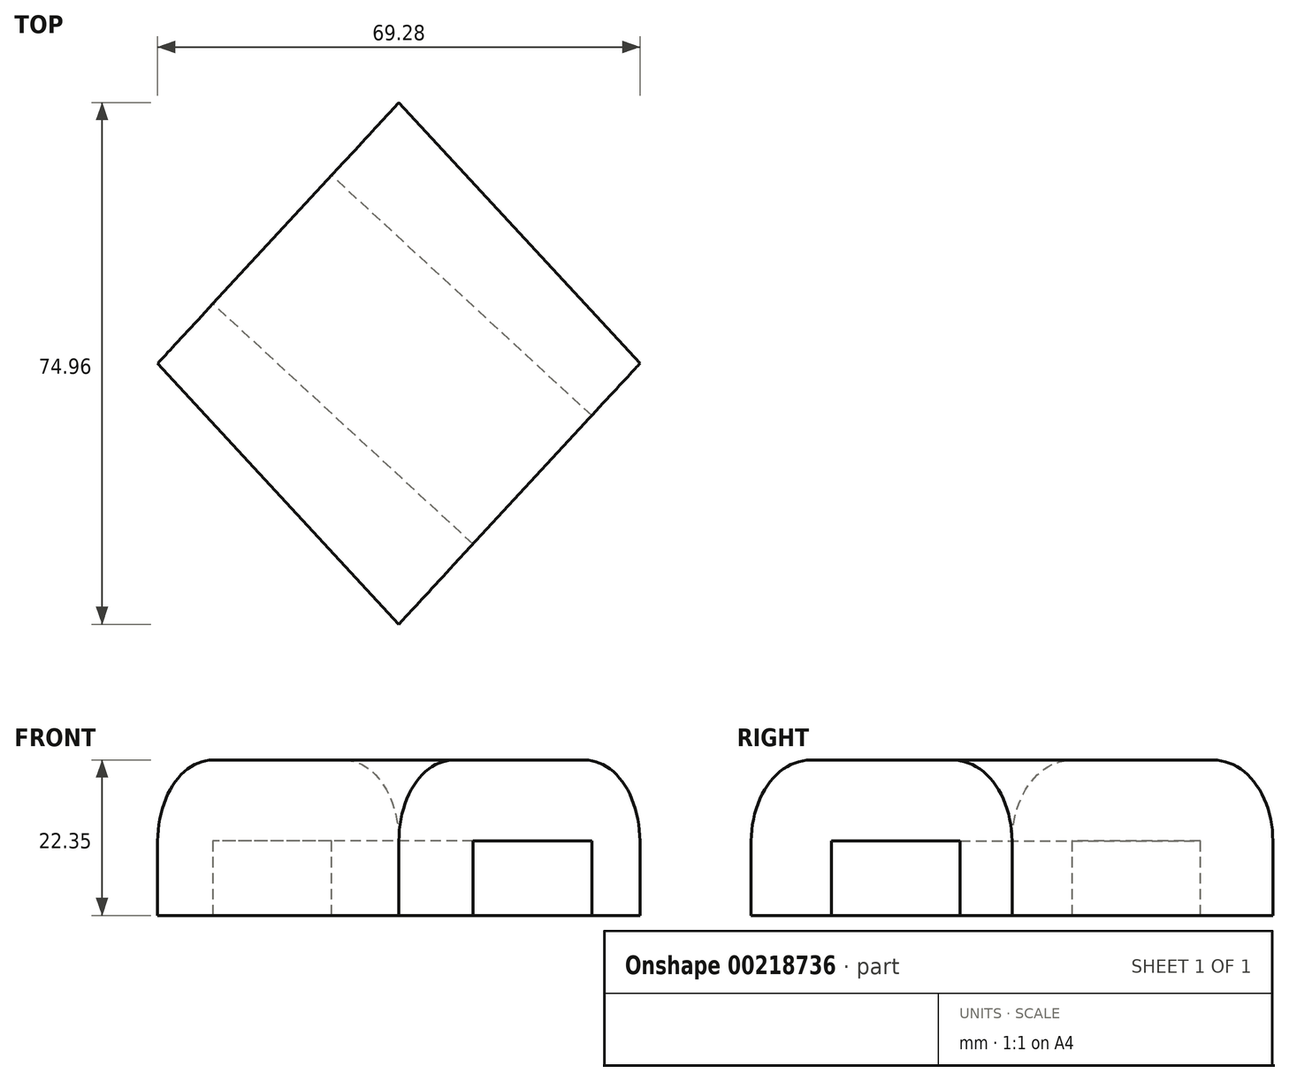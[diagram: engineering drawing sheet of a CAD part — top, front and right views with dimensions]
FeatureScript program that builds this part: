
annotation { "Feature Type Name" : "Feature", "Feature Type Description" : "" }
export const myFeature = defineFeature(function(context is Context, id is Id, definition is map)
    precondition{}
    {
        {
            var Q0;
            Q0=qCreatedBy(makeId("Top.planeOp"),FACE);
            var sketch = newSketch(context, id + "F0", { "sketchPlane" : qUnion([Q0])});
            skLineSegment(sketch, "E0", {"start": v(-34.64, 0) * mm, "end": v(0, 37.48) * mm});
            skLineSegment(sketch, "E1", {"start": v(0, 37.48) * mm, "end": v(34.64, 0) * mm});
            skLineSegment(sketch, "E2", {"start": v(34.64, 0) * mm, "end": v(0, -37.48) * mm});
            skLineSegment(sketch, "E3", {"start": v(0, -37.48) * mm, "end": v(-34.64, 0) * mm});
            skSolve(sketch);
        }
        {
            var Q0;
            Q0=makeQuery(id+"F0.imprint","IMPRINT",FACE,{"disambiguationData":[TD([[makeQuery(id+"F0.imprint","IMPRINT",EDGE,{"derivedFrom":sQuery(id+"F0.wireOp",EDGE,"E0")}),-1.0]])]});
            extrude(context, id + "F1", {"entities" : qUnion([Q0]), "depth" : 22.35 * mm});
        }
        {
            var Q0;
            Q0=makeQuery(id+"F1.opExtrude","CAP_EDGE",EDGE,{"disambiguationData":[OSD([sQuery(id+"F0.wireOp",EDGE,"E3")])],"isStart":false});
            var Q1;
            Q1=makeQuery(id+"F1.opExtrude","CAP_EDGE",EDGE,{"disambiguationData":[OSD([sQuery(id+"F0.wireOp",EDGE,"E1")])],"isStart":false});
            fillet(context, id + "F2", {"entities" : qUnion([Q0, Q1]), "radius" : 11.65 * mm, "tangentPropagation" : true, "allowEdgeOverflow" : false});
        }
        {
            var Q0;
            Q0=makeQuery(id+"F1.opExtrude","SWEPT_FACE",FACE,{"disambiguationData":[OSD([sQuery(id+"F0.wireOp",EDGE,"E0")])]});
            var sketch = newSketch(context, id + "F3", { "sketchPlane" : qUnion([Q0])});
            skLineSegment(sketch, "E4", {"start": v(-13.3, 0) * mm, "end": v(-13.3, 10.7) * mm});
            skLineSegment(sketch, "E5", {"start": v(-13.3, 10.7) * mm, "end": v(11.83, 10.7) * mm});
            skLineSegment(sketch, "E6", {"start": v(11.83, 10.7) * mm, "end": v(11.83, 0) * mm});
            skLineSegment(sketch, "E7", {"start": v(11.83, 0) * mm, "end": v(-13.3, 0) * mm});
            skSolve(sketch);
        }
        {
            var Q0;
            Q0=makeQuery(id+"F3.imprint","IMPRINT",FACE,{"disambiguationData":[TD([[makeQuery(id+"F3.imprint","IMPRINT",EDGE,{"derivedFrom":sQuery(id+"F3.wireOp",EDGE,"E4")}),-1.0]])]});
            extrude(context, id + "F5", {"entities" : qUnion([Q0]), "operationType" : NewBodyOperationType.REMOVE, "endBound" : BoundingType.THROUGH_ALL, "oppositeDirection" : true, "depth" : 25.4 * mm});
        }
    });
